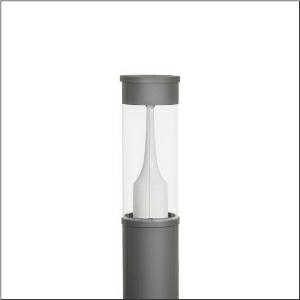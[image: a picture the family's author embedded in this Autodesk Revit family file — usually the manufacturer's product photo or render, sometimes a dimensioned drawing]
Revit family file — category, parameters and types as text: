
# Revit family: city-light_120_iq___p1_0a_5xa5285ff14h_303b
name_source: partatom
category: Lighting Fixtures
units: mm (PartAtom-declared; Revit-internal decimal feet)

## family parameters
Cut with Voids When Loaded = No
Host = Face
Light Source = No
Part Type = Normal
Room Calculation Point = No
Round Connector Dimension = Use Diameter
Shared = No

## types (1)
- --- (1 x LED, 1510 lm, 10.5 W, 3000K)
    Apparent Load = 11 VA
    CIE Flux Codes = 32 61 90 93 100
    Color Rendering = 70
    Color Temperature = 3000K
    Default Elevation = 1800 mm
    Description = City-Light 120 iQ, bollard luminaire, Module 540 iQ-SR, primary light control with 3 zone facetted reflector, of plastic, silver coated, highly specular, structured, primary optical cover: cover, of PMMA, transparent, light distribution: P1.0a, primary light characteristic: strongly asymmetric, LED, High Power LED, rated luminous flux: 1.510lm, luminous efficacy: 144lm/W, light colour: 730, colour temperature: 3000K, control gear: iQ Street-Remote, control: Auto-Match, Temp-Guard, Lumen-Switch, Night-Set, Smart-Wire, Light-Fading, Desk-Remote (wireless, voltage-free reading and setting of iQ features in the workshop via application-optimized NFC function/RFID function), optimised constant luminous flux control (CLO 2.0), Street-Remote, pre-setting: logarithmic dimming characteristic, with terminal, 6-pole, max. 2.5mm², mains connection: 230..240V, AC, 50/60Hz, start of lifetime: 11W, end of service life: 11W, reduction: 5W, luminaire housing, cylindrical, of extruded aluminium section, coated, Siteco® metallic grey (DB 702S), length: 1.200mm, diameter: 200mm, Module 540 iQ-SR, traffic white (RAL 9016), equipment: standard, protection rating (complete): IP54, insulation class (complete): insulation class II (safety insulation), certification: CE, ENEC, VDE, packaging unit: 1 piece

Light Distribution: P1.0a
    Height = 500 mm
    Lamp = 1 x LED
    Lamp Light Flux = 1510 lm
    Lamp Power = 10.5 W
    Lamp count = 1
    Length = 200 mm  [stored 0.656168 ft]
    Luminous efficacy = 144 lm/W
    Manufacturer = Siteco
    ModVariant = No
    Model = 5XA5285FF14H
    Mounting Place = Floor
    Mounting Type = Freestanding
    Number of Poles = 1
    OnlyDefault = Yes
    Power Factor = 1
    Product Name = City-Light 120 iQ | P1.0a
    Product group = bollard luminaire
    ProductGroupID = 1304
    Protection Class = Protection class II
    Protection Degree = IP 54
    RLX_Detail_Level = 1
    RLX_Emergency_Light_Flux = 0 lm
    RLX_Emergency_Type = 0
    RLX_Emergency_Type_DB = No
    RlxData = <blob elided: 52821 chars, md5=ff71404b>
    Socket = socket
    Standby Power = 0 W
    System Light Flux = 1510 lm
    System Power = 11 W
    Type Comments = factory setting: luminous flux: 100 % | dim-lin: 254 | 419 mA
    Type Image = l_1006922.jpg
    URL = http://relux.com
    VarID = @adj_181061
    Voltage = 0 V
    Weight = 0.00 kg
    Width = 0 mm  [stored 0 ft]

note: [stored X ft] marks values corroborated as IEEE doubles in the binary element streams (Revit-internal decimal feet)

## geometry (parser evidence)
native form markers: Blend x4, Sweep x13
no freeform markers — native parametric forms only
